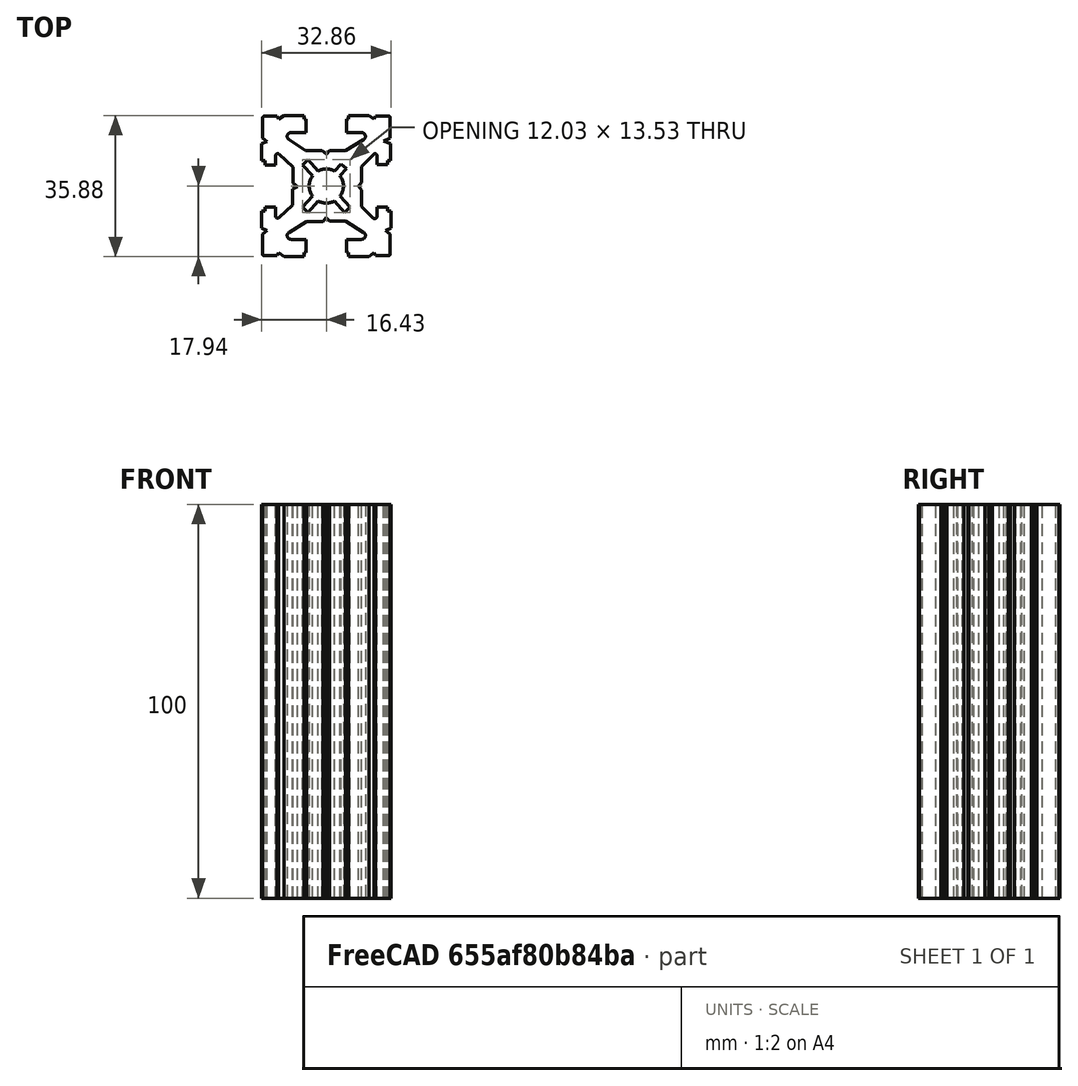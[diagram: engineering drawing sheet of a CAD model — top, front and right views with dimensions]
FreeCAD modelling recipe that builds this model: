
FCSTD DOCUMENT  (FreeCAD 0.17R13509 (Git))
Label: Profile Bosh 30x30mm
License: All rights reserved
LicenseURL: http://en.wikipedia.org/wiki/All_rights_reserved
objects: Sketcher::SketchObject×2, PartDesign::Pad×1, PartDesign::Body×1, App::Part×1
note: 5 computed .brp shape members not serialized (recipe doc carries the construction recipe); baked Part::Feature solids carry a one-line shape summary decoded from their .brp

FEATURE [Sketcher::SketchObject] Sketch
  sketch-geometry (116):
    g0: BSplineCurve PolesCount=2 KnotsCount=2 Degree=1 IsPeriodic=0
    g1: BSplineCurve PolesCount=2 KnotsCount=2 Degree=1 IsPeriodic=0
    g2: BSplineCurve PolesCount=2 KnotsCount=2 Degree=1 IsPeriodic=0
    g3: BSplineCurve PolesCount=3 KnotsCount=2 Degree=2 IsPeriodic=0
    g4: BSplineCurve PolesCount=3 KnotsCount=2 Degree=2 IsPeriodic=0
    g5: BSplineCurve PolesCount=3 KnotsCount=2 Degree=2 IsPeriodic=0
    g6: BSplineCurve PolesCount=3 KnotsCount=2 Degree=2 IsPeriodic=0
    g7: BSplineCurve PolesCount=3 KnotsCount=2 Degree=2 IsPeriodic=0
    g8: BSplineCurve PolesCount=3 KnotsCount=2 Degree=2 IsPeriodic=0
    g9: BSplineCurve PolesCount=3 KnotsCount=2 Degree=2 IsPeriodic=0
    g10: BSplineCurve PolesCount=3 KnotsCount=2 Degree=2 IsPeriodic=0
    g11: BSplineCurve PolesCount=2 KnotsCount=2 Degree=1 IsPeriodic=0
    g12: BSplineCurve PolesCount=2 KnotsCount=2 Degree=1 IsPeriodic=0
    g13: BSplineCurve PolesCount=2 KnotsCount=2 Degree=1 IsPeriodic=0
    g14: BSplineCurve PolesCount=2 KnotsCount=2 Degree=1 IsPeriodic=0
    g15: BSplineCurve PolesCount=2 KnotsCount=2 Degree=1 IsPeriodic=0
    g16: BSplineCurve PolesCount=2 KnotsCount=2 Degree=1 IsPeriodic=0
    g17: BSplineCurve PolesCount=2 KnotsCount=2 Degree=1 IsPeriodic=0
    g18: BSplineCurve PolesCount=2 KnotsCount=2 Degree=1 IsPeriodic=0
    g19: BSplineCurve PolesCount=2 KnotsCount=2 Degree=1 IsPeriodic=0
    g20: BSplineCurve PolesCount=2 KnotsCount=2 Degree=1 IsPeriodic=0
    g21: BSplineCurve PolesCount=2 KnotsCount=2 Degree=1 IsPeriodic=0
    g22: BSplineCurve PolesCount=2 KnotsCount=2 Degree=1 IsPeriodic=0
    g23: BSplineCurve PolesCount=2 KnotsCount=2 Degree=1 IsPeriodic=0
    g24: BSplineCurve PolesCount=2 KnotsCount=2 Degree=1 IsPeriodic=0
    g25: BSplineCurve PolesCount=2 KnotsCount=2 Degree=1 IsPeriodic=0
    g26: BSplineCurve PolesCount=2 KnotsCount=2 Degree=1 IsPeriodic=0
    g27: BSplineCurve PolesCount=2 KnotsCount=2 Degree=1 IsPeriodic=0
    g28: BSplineCurve PolesCount=2 KnotsCount=2 Degree=1 IsPeriodic=0
    g29: BSplineCurve PolesCount=2 KnotsCount=2 Degree=1 IsPeriodic=0
    g30: BSplineCurve PolesCount=2 KnotsCount=2 Degree=1 IsPeriodic=0
    g31: BSplineCurve PolesCount=2 KnotsCount=2 Degree=1 IsPeriodic=0
    g32: BSplineCurve PolesCount=2 KnotsCount=2 Degree=1 IsPeriodic=0
    g33: BSplineCurve PolesCount=2 KnotsCount=2 Degree=1 IsPeriodic=0
    g34: BSplineCurve PolesCount=2 KnotsCount=2 Degree=1 IsPeriodic=0
    g35: BSplineCurve PolesCount=2 KnotsCount=2 Degree=1 IsPeriodic=0
    g36: BSplineCurve PolesCount=2 KnotsCount=2 Degree=1 IsPeriodic=0
    g37: BSplineCurve PolesCount=2 KnotsCount=2 Degree=1 IsPeriodic=0
    g38: BSplineCurve PolesCount=2 KnotsCount=2 Degree=1 IsPeriodic=0
    g39: BSplineCurve PolesCount=2 KnotsCount=2 Degree=1 IsPeriodic=0
    g40: BSplineCurve PolesCount=2 KnotsCount=2 Degree=1 IsPeriodic=0
    g41: BSplineCurve PolesCount=2 KnotsCount=2 Degree=1 IsPeriodic=0
    g42: BSplineCurve PolesCount=2 KnotsCount=2 Degree=1 IsPeriodic=0
    g43: BSplineCurve PolesCount=2 KnotsCount=2 Degree=1 IsPeriodic=0
    g44: BSplineCurve PolesCount=3 KnotsCount=2 Degree=2 IsPeriodic=0
    g45: BSplineCurve PolesCount=2 KnotsCount=2 Degree=1 IsPeriodic=0
    g46: BSplineCurve PolesCount=2 KnotsCount=2 Degree=1 IsPeriodic=0
    g47: BSplineCurve PolesCount=2 KnotsCount=2 Degree=1 IsPeriodic=0
    g48: BSplineCurve PolesCount=2 KnotsCount=2 Degree=1 IsPeriodic=0
    g49: BSplineCurve PolesCount=3 KnotsCount=2 Degree=2 IsPeriodic=0
    g50: BSplineCurve PolesCount=2 KnotsCount=2 Degree=1 IsPeriodic=0
    g51: BSplineCurve PolesCount=3 KnotsCount=2 Degree=2 IsPeriodic=0
    g52: BSplineCurve PolesCount=3 KnotsCount=2 Degree=2 IsPeriodic=0
    g53: BSplineCurve PolesCount=3 KnotsCount=2 Degree=2 IsPeriodic=0
    g54: BSplineCurve PolesCount=2 KnotsCount=2 Degree=1 IsPeriodic=0
    g55: BSplineCurve PolesCount=2 KnotsCount=2 Degree=1 IsPeriodic=0
    g56: BSplineCurve PolesCount=2 KnotsCount=2 Degree=1 IsPeriodic=0
    g57: BSplineCurve PolesCount=2 KnotsCount=2 Degree=1 IsPeriodic=0
    g58: BSplineCurve PolesCount=3 KnotsCount=2 Degree=2 IsPeriodic=0
    g59: BSplineCurve PolesCount=3 KnotsCount=2 Degree=2 IsPeriodic=0
    g60: BSplineCurve PolesCount=3 KnotsCount=2 Degree=2 IsPeriodic=0
    g61: BSplineCurve PolesCount=2 KnotsCount=2 Degree=1 IsPeriodic=0
    g62: BSplineCurve PolesCount=2 KnotsCount=2 Degree=1 IsPeriodic=0
    g63: BSplineCurve PolesCount=2 KnotsCount=2 Degree=1 IsPeriodic=0
    g64: BSplineCurve PolesCount=2 KnotsCount=2 Degree=1 IsPeriodic=0
    g65: BSplineCurve PolesCount=2 KnotsCount=2 Degree=1 IsPeriodic=0
    g66: BSplineCurve PolesCount=2 KnotsCount=2 Degree=1 IsPeriodic=0
    g67: BSplineCurve PolesCount=2 KnotsCount=2 Degree=1 IsPeriodic=0
    g68: BSplineCurve PolesCount=2 KnotsCount=2 Degree=1 IsPeriodic=0
    g69: BSplineCurve PolesCount=2 KnotsCount=2 Degree=1 IsPeriodic=0
    g70: BSplineCurve PolesCount=2 KnotsCount=2 Degree=1 IsPeriodic=0
    g71: BSplineCurve PolesCount=2 KnotsCount=2 Degree=1 IsPeriodic=0
    g72: BSplineCurve PolesCount=2 KnotsCount=2 Degree=1 IsPeriodic=0
    g73: BSplineCurve PolesCount=2 KnotsCount=2 Degree=1 IsPeriodic=0
    g74: BSplineCurve PolesCount=2 KnotsCount=2 Degree=1 IsPeriodic=0
    g75: BSplineCurve PolesCount=2 KnotsCount=2 Degree=1 IsPeriodic=0
    g76: BSplineCurve PolesCount=2 KnotsCount=2 Degree=1 IsPeriodic=0
    g77: BSplineCurve PolesCount=2 KnotsCount=2 Degree=1 IsPeriodic=0
    g78: BSplineCurve PolesCount=2 KnotsCount=2 Degree=1 IsPeriodic=0
    g79: BSplineCurve PolesCount=2 KnotsCount=2 Degree=1 IsPeriodic=0
    g80: BSplineCurve PolesCount=2 KnotsCount=2 Degree=1 IsPeriodic=0
    g81: BSplineCurve PolesCount=2 KnotsCount=2 Degree=1 IsPeriodic=0
    g82: BSplineCurve PolesCount=2 KnotsCount=2 Degree=1 IsPeriodic=0
    g83: BSplineCurve PolesCount=2 KnotsCount=2 Degree=1 IsPeriodic=0
    g84: BSplineCurve PolesCount=2 KnotsCount=2 Degree=1 IsPeriodic=0
    g85: BSplineCurve PolesCount=2 KnotsCount=2 Degree=1 IsPeriodic=0
    g86: BSplineCurve PolesCount=2 KnotsCount=2 Degree=1 IsPeriodic=0
    g87: BSplineCurve PolesCount=2 KnotsCount=2 Degree=1 IsPeriodic=0
    g88: BSplineCurve PolesCount=2 KnotsCount=2 Degree=1 IsPeriodic=0
    g89: BSplineCurve PolesCount=2 KnotsCount=2 Degree=1 IsPeriodic=0
    g90: BSplineCurve PolesCount=2 KnotsCount=2 Degree=1 IsPeriodic=0
    g91: BSplineCurve PolesCount=2 KnotsCount=2 Degree=1 IsPeriodic=0
    g92: BSplineCurve PolesCount=2 KnotsCount=2 Degree=1 IsPeriodic=0
    g93: BSplineCurve PolesCount=2 KnotsCount=2 Degree=1 IsPeriodic=0
    g94: BSplineCurve PolesCount=2 KnotsCount=2 Degree=1 IsPeriodic=0
    g95: BSplineCurve PolesCount=2 KnotsCount=2 Degree=1 IsPeriodic=0
    g96: BSplineCurve PolesCount=2 KnotsCount=2 Degree=1 IsPeriodic=0
    g97: BSplineCurve PolesCount=2 KnotsCount=2 Degree=1 IsPeriodic=0
    g98: BSplineCurve PolesCount=2 KnotsCount=2 Degree=1 IsPeriodic=0
    g99: BSplineCurve PolesCount=2 KnotsCount=2 Degree=1 IsPeriodic=0
    g100: BSplineCurve PolesCount=2 KnotsCount=2 Degree=1 IsPeriodic=0
    g101: BSplineCurve PolesCount=2 KnotsCount=2 Degree=1 IsPeriodic=0
    g102: BSplineCurve PolesCount=2 KnotsCount=2 Degree=1 IsPeriodic=0
    g103: BSplineCurve PolesCount=2 KnotsCount=2 Degree=1 IsPeriodic=0
    g104: BSplineCurve PolesCount=2 KnotsCount=2 Degree=1 IsPeriodic=0
    g105: BSplineCurve PolesCount=2 KnotsCount=2 Degree=1 IsPeriodic=0
    g106: BSplineCurve PolesCount=2 KnotsCount=2 Degree=1 IsPeriodic=0
    g107: BSplineCurve PolesCount=2 KnotsCount=2 Degree=1 IsPeriodic=0
    g108: BSplineCurve PolesCount=2 KnotsCount=2 Degree=1 IsPeriodic=0
    g109: BSplineCurve PolesCount=2 KnotsCount=2 Degree=1 IsPeriodic=0
    g110: BSplineCurve PolesCount=2 KnotsCount=2 Degree=1 IsPeriodic=0
    g111: BSplineCurve PolesCount=2 KnotsCount=2 Degree=1 IsPeriodic=0
    g112: BSplineCurve PolesCount=2 KnotsCount=2 Degree=1 IsPeriodic=0
    g113: BSplineCurve PolesCount=2 KnotsCount=2 Degree=1 IsPeriodic=0
    g114: BSplineCurve PolesCount=2 KnotsCount=2 Degree=1 IsPeriodic=0
    g115: BSplineCurve PolesCount=2 KnotsCount=2 Degree=1 IsPeriodic=0
FEATURE [Sketcher::SketchObject] Sketch001
  MapMode = 5
  Support = -> [XY_Plane001]
  sketch-geometry (121):
    g0: LineSegment [constr] StartX=0 StartY=0 StartZ=0 EndX=0 EndY=8.13256 EndZ=0
    g1: LineSegment [constr] StartX=8.13256 StartY=0 StartZ=0 EndX=0 EndY=0 EndZ=0
    g2: LineSegment StartX=0 StartY=8.13256 StartZ=0 EndX=0.863984 EndY=8.96505 EndZ=0
    g3: LineSegment StartX=0.863984 StartY=8.96505 StartZ=0 EndX=4.93425 EndY=8.96505 EndZ=0
    g4: LineSegment StartX=4.93425 StartY=8.96505 StartZ=0 EndX=9.48637 EndY=11.797 EndZ=0
    g5: LineSegment StartX=8.98459 StartY=13.5535 StartZ=0 EndX=5.15812 EndY=13.5535 EndZ=0
    g6: LineSegment StartX=5.15812 StartY=13.5535 StartZ=0 EndX=5.15812 EndY=16.9407 EndZ=0
    g7: LineSegment StartX=5.15812 StartY=16.9407 StartZ=0 EndX=5.6531 EndY=16.9407 EndZ=0
    g8: LineSegment StartX=5.6531 StartY=16.9407 StartZ=0 EndX=5.6531 EndY=17.9363 EndZ=0
    g9: LineSegment StartX=5.6531 StartY=17.9363 StartZ=0 EndX=10.7923 EndY=17.9363 EndZ=0
    g10: LineSegment StartX=10.7923 StartY=17.9363 StartZ=0 EndX=12.0719 EndY=16.9647 EndZ=0
    g11: LineSegment StartX=12.0719 StartY=16.9647 StartZ=0 EndX=12.5221 EndY=17.7592 EndZ=0
    g12: LineSegment StartX=12.5221 StartY=17.7592 StartZ=0 EndX=15.8708 EndY=17.7592 EndZ=0
    g13: LineSegment StartX=16.246 StartY=17.384 StartZ=0 EndX=16.246 EndY=12.1724 EndZ=0
    g14: LineSegment StartX=16.246 StartY=12.1724 StartZ=0 EndX=14.4892 EndY=11.3845 EndZ=0
    g15: LineSegment StartX=14.4892 StartY=11.3845 StartZ=0 EndX=16.2567 EndY=10.735 EndZ=0
    g16: LineSegment StartX=16.2567 StartY=10.735 StartZ=0 EndX=16.2567 EndY=6.42108 EndZ=0
    g17: LineSegment StartX=16.2567 StartY=6.42108 StartZ=0 EndX=15.6194 EndY=6.42108 EndZ=0
    g18: ArcOfCircle CenterX=15.8708 CenterY=17.384 CenterZ=0 NormalX=0 NormalY=0 NormalZ=1 AngleXU=0 Radius=0.375206 StartAngle=0 EndAngle=1.5708
    g19: ArcOfCircle CenterX=12.38 CenterY=7.66792 CenterZ=0 NormalX=0 NormalY=0 NormalZ=1 AngleXU=0 Radius=0.511001 StartAngle=0 EndAngle=2.35619
    g20: ArcOfCircle CenterX=8.98459 CenterY=12.6036 CenterZ=0 NormalX=0 NormalY=0 NormalZ=1 AngleXU=0 Radius=0.949916 StartAngle=5.26891 EndAngle=7.85398
    g21: LineSegment StartX=15.6194 StartY=6.42108 StartZ=0 EndX=15.6194 EndY=5.37886 EndZ=0
    g22: LineSegment StartX=15.6194 StartY=5.37886 StartZ=0 EndX=12.891 EndY=5.37886 EndZ=0
    g23: LineSegment StartX=12.891 StartY=5.37886 StartZ=0 EndX=12.891 EndY=7.66792 EndZ=0
    g24: LineSegment StartX=12.0187 StartY=8.02925 StartZ=0 EndX=8.94375 EndY=4.95429 EndZ=0
    g25: LineSegment StartX=8.94375 StartY=4.95429 StartZ=0 EndX=8.94375 EndY=0.884017 EndZ=0
    g26: LineSegment StartX=8.94375 StartY=0.884017 StartZ=0 EndX=8.13256 EndY=0 EndZ=0
    g27: ArcOfCircle CenterX=0 CenterY=0 CenterZ=0 NormalX=0 NormalY=0 NormalZ=1 AngleXU=0 Radius=4.34461 StartAngle=1.06729 EndAngle=2.0743
    g28: LineSegment StartX=-2.09626 StartY=3.80544 StartZ=0 EndX=-4.58638 EndY=6.76319 EndZ=0
    g29: LineSegment StartX=-4.58638 StartY=6.76319 StartZ=0 EndX=-6.01301 EndY=5.3625 EndZ=0
    g30: LineSegment StartX=-6.01301 StartY=5.3625 StartZ=0 EndX=-3.47101 EndY=2.61299 EndZ=0
    g31: LineSegment StartX=2.09626 StartY=3.80544 StartZ=0 EndX=3.70713 EndY=5.62355 EndZ=0
    g32: LineSegment StartX=3.70713 StartY=5.62355 StartZ=0 EndX=5.08583 EndY=4.45696 EndZ=0
    g33: LineSegment StartX=5.08583 StartY=4.45696 StartZ=0 EndX=3.47101 EndY=2.61299 EndZ=0
    g34: LineSegment StartX=2.09626 StartY=-3.80544 StartZ=0 EndX=4.58638 EndY=-6.76319 EndZ=0
    g35: LineSegment StartX=4.58638 StartY=-6.76319 StartZ=0 EndX=6.01301 EndY=-5.3625 EndZ=0
    g36: LineSegment StartX=6.01301 StartY=-5.3625 StartZ=0 EndX=3.47101 EndY=-2.61299 EndZ=0
    g37: LineSegment StartX=-2.09626 StartY=-3.80544 StartZ=0 EndX=-4.58638 EndY=-6.76319 EndZ=0
    g38: LineSegment StartX=-6.01301 StartY=-5.3625 StartZ=0 EndX=-3.47101 EndY=-2.61299 EndZ=0
    g39: LineSegment StartX=-4.58638 StartY=-6.76319 StartZ=0 EndX=-6.01301 EndY=-5.3625 EndZ=0
    g40: ArcOfCircle CenterX=0 CenterY=0 CenterZ=0 NormalX=0 NormalY=0 NormalZ=1 AngleXU=0 Radius=4.34461 StartAngle=2.4963 EndAngle=3.78689
    g41: ArcOfCircle CenterX=0 CenterY=0 CenterZ=0 NormalX=0 NormalY=0 NormalZ=1 AngleXU=0 Radius=4.34461 StartAngle=4.20889 EndAngle=5.21589
    g42: ArcOfCircle CenterX=0 CenterY=0 CenterZ=0 NormalX=0 NormalY=0 NormalZ=1 AngleXU=0 Radius=4.34461 StartAngle=5.63789 EndAngle=6.92848
    g43: LineSegment [constr] StartX=8.94375 StartY=4.95429 StartZ=0 EndX=10.2141 EndY=4.95429 EndZ=0
    g44: LineSegment StartX=0 StartY=8.13256 StartZ=0 EndX=-1.12485 EndY=9.01316 EndZ=0
    g45: LineSegment StartX=-1.12485 StartY=9.01316 StartZ=0 EndX=-5.23766 EndY=9.01316 EndZ=0
    g46: LineSegment StartX=-5.23766 StartY=9.01316 StartZ=0 EndX=-9.50558 EndY=11.8091 EndZ=0
    g47: LineSegment StartX=-8.98499 StartY=13.5537 StartZ=0 EndX=-5.15812 EndY=13.5537 EndZ=0
    g48: LineSegment StartX=-5.15812 StartY=13.5537 StartZ=0 EndX=-5.15812 EndY=16.9407 EndZ=0
    g49: LineSegment StartX=-5.15812 StartY=16.9407 StartZ=0 EndX=-5.6531 EndY=16.9407 EndZ=0
    g50: LineSegment StartX=-5.6531 StartY=16.9407 StartZ=0 EndX=-5.6531 EndY=17.9363 EndZ=0
    g51: LineSegment StartX=-5.6531 StartY=17.9363 StartZ=0 EndX=-10.7923 EndY=17.9363 EndZ=0
    g52: LineSegment StartX=-10.7923 StartY=17.9363 StartZ=0 EndX=-12.0719 EndY=16.9647 EndZ=0
    g53: LineSegment StartX=-12.0719 StartY=16.9647 StartZ=0 EndX=-12.5221 EndY=17.7251 EndZ=0
    g54: LineSegment StartX=-12.5221 StartY=17.7251 StartZ=0 EndX=-15.8282 EndY=17.7251 EndZ=0
    g55: LineSegment StartX=-16.1524 StartY=17.401 StartZ=0 EndX=-16.1524 EndY=12.1805 EndZ=0
    g56: LineSegment StartX=-16.1524 StartY=12.1805 StartZ=0 EndX=-14.9921 EndY=11.3367 EndZ=0
    g57: LineSegment StartX=-14.9921 StartY=11.3367 StartZ=0 EndX=-16.4328 EndY=10.7136 EndZ=0
    g58: LineSegment StartX=-16.4328 StartY=10.7136 StartZ=0 EndX=-16.4328 EndY=6.42108 EndZ=0
    g59: LineSegment StartX=-16.4328 StartY=6.42108 StartZ=0 EndX=-15.6194 EndY=6.42108 EndZ=0
    g60: ArcOfCircle CenterX=-15.8282 CenterY=17.401 CenterZ=0 NormalX=0 NormalY=0 NormalZ=1 AngleXU=0 Radius=0.324122 StartAngle=1.5708 EndAngle=3.14159
    g61: ArcOfCircle CenterX=-8.98499 CenterY=12.6037 CenterZ=0 NormalX=0 NormalY=0 NormalZ=1 AngleXU=0 Radius=0.949992 StartAngle=1.5708 EndAngle=4.13243
    g62: LineSegment StartX=-15.6194 StartY=6.42108 StartZ=0 EndX=-15.6194 EndY=5.3545 EndZ=0
    g63: LineSegment StartX=-15.6194 StartY=5.3545 StartZ=0 EndX=-12.8911 EndY=5.3545 EndZ=0
    g64: ArcOfCircle CenterX=-12.3588 CenterY=7.67266 CenterZ=0 NormalX=0 NormalY=0 NormalZ=1 AngleXU=0 Radius=0.532302 StartAngle=0.822691 EndAngle=3.14117
    g65: LineSegment StartX=-11.9967 StartY=8.06282 StartZ=0 EndX=-8.50501 EndY=4.82235 EndZ=0
    g66: LineSegment StartX=-8.50501 StartY=4.82235 StartZ=0 EndX=-8.50501 EndY=0.709539 EndZ=0
    g67: LineSegment StartX=-8.50501 StartY=0.709539 StartZ=0 EndX=-7.362 EndY=-0.147361 EndZ=0
    g68: LineSegment [constr] StartX=-0.0366578 StartY=0 StartZ=0 EndX=-0.0366578 EndY=-7.97192 EndZ=0
    g69: LineSegment StartX=-0.0366578 StartY=-7.97192 StartZ=0 EndX=0.851967 EndY=-8.95417 EndZ=0
    g70: LineSegment StartX=0.851967 StartY=-8.95417 StartZ=0 EndX=4.95077 EndY=-8.95417 EndZ=0
    g71: LineSegment StartX=4.95077 StartY=-8.95417 StartZ=0 EndX=9.48868 EndY=-11.7973 EndZ=0
    g72: LineSegment StartX=8.98403 StartY=-13.5532 StartZ=0 EndX=5.15812 EndY=-13.5532 EndZ=0
    g73: LineSegment StartX=5.15812 StartY=-13.5532 StartZ=0 EndX=5.15812 EndY=-16.9407 EndZ=0
    g74: LineSegment StartX=5.15812 StartY=-16.9407 StartZ=0 EndX=5.6531 EndY=-16.9407 EndZ=0
    g75: LineSegment StartX=5.6531 StartY=-16.9407 StartZ=0 EndX=5.6531 EndY=-17.9363 EndZ=0
    g76: LineSegment StartX=5.6531 StartY=-17.9363 StartZ=0 EndX=10.7923 EndY=-17.9363 EndZ=0
    g77: LineSegment StartX=10.7923 StartY=-17.9363 StartZ=0 EndX=12.0719 EndY=-16.9647 EndZ=0
    g78: LineSegment StartX=12.0719 StartY=-16.9647 StartZ=0 EndX=12.5221 EndY=-17.7251 EndZ=0
    g79: LineSegment StartX=12.5221 StartY=-17.7251 StartZ=0 EndX=15.8282 EndY=-17.7251 EndZ=0
    g80: LineSegment StartX=16.1524 StartY=-17.401 StartZ=0 EndX=16.1524 EndY=-12.1805 EndZ=0
    g81: LineSegment StartX=16.1524 StartY=-12.1805 StartZ=0 EndX=14.9921 EndY=-11.3367 EndZ=0
    g82: LineSegment StartX=14.9921 StartY=-11.3367 StartZ=0 EndX=16.4328 EndY=-10.7136 EndZ=0
    g83: LineSegment StartX=16.4328 StartY=-10.7136 StartZ=0 EndX=16.4328 EndY=-6.42108 EndZ=0
    g84: ArcOfCircle CenterX=15.8282 CenterY=-17.401 CenterZ=0 NormalX=0 NormalY=0 NormalZ=1 AngleXU=0 Radius=0.324122 StartAngle=4.71239 EndAngle=6.28319
    g85: ArcOfCircle CenterX=12.2781 CenterY=-7.67162 CenterZ=0 NormalX=0 NormalY=0 NormalZ=1 AngleXU=0 Radius=0.613906 StartAngle=3.92699 EndAngle=6.28319
    g86: ArcOfCircle CenterX=8.98403 CenterY=-12.6027 CenterZ=0 NormalX=0 NormalY=0 NormalZ=1 AngleXU=0 Radius=0.950502 StartAngle=4.71239 EndAngle=7.29429
    g87: LineSegment StartX=12.892 StartY=-5.37886 StartZ=0 EndX=12.892 EndY=-7.67162 EndZ=0
    g88: LineSegment StartX=11.844 StartY=-8.10572 StartZ=0 EndX=8.9097 EndY=-5.17142 EndZ=0
    g89: LineSegment StartX=-0.0366578 StartY=-7.97192 StartZ=0 EndX=-0.845387 EndY=-8.98483 EndZ=0
    g90: LineSegment StartX=-0.845387 StartY=-8.98483 StartZ=0 EndX=-4.96492 EndY=-8.98483 EndZ=0
    g91: LineSegment StartX=-4.96492 StartY=-8.98483 StartZ=0 EndX=-9.48593 EndY=-11.7955 EndZ=0
    g92: LineSegment StartX=-8.98406 StartY=-13.5533 StartZ=0 EndX=-5.15812 EndY=-13.5533 EndZ=0
    g93: LineSegment StartX=-5.15812 StartY=-13.5533 StartZ=0 EndX=-5.15812 EndY=-16.9407 EndZ=0
    g94: LineSegment StartX=-5.15812 StartY=-16.9407 StartZ=0 EndX=-5.6531 EndY=-16.9407 EndZ=0
    g95: LineSegment StartX=-5.6531 StartY=-16.9407 StartZ=0 EndX=-5.6531 EndY=-17.9363 EndZ=0
    g96: LineSegment StartX=-5.6531 StartY=-17.9363 StartZ=0 EndX=-10.7923 EndY=-17.9363 EndZ=0
    g97: LineSegment StartX=-10.7923 StartY=-17.9363 StartZ=0 EndX=-12.0719 EndY=-16.9647 EndZ=0
    g98: LineSegment StartX=-12.0719 StartY=-16.9647 StartZ=0 EndX=-12.5221 EndY=-17.7251 EndZ=0
    g99: LineSegment StartX=-12.5221 StartY=-17.7251 StartZ=0 EndX=-15.8282 EndY=-17.7251 EndZ=0
    g100: LineSegment StartX=-16.1524 StartY=-17.401 StartZ=0 EndX=-16.1524 EndY=-12.1805 EndZ=0
    g101: LineSegment StartX=-16.1524 StartY=-12.1805 StartZ=0 EndX=-14.9921 EndY=-11.3367 EndZ=0
    g102: LineSegment StartX=-14.9921 StartY=-11.3367 StartZ=0 EndX=-16.4328 EndY=-10.7136 EndZ=0
    g103: LineSegment StartX=-16.4328 StartY=-10.7136 StartZ=0 EndX=-16.4328 EndY=-6.42108 EndZ=0
    g104: ArcOfCircle CenterX=-15.8282 CenterY=-17.401 CenterZ=0 NormalX=0 NormalY=0 NormalZ=1 AngleXU=0 Radius=0.324122 StartAngle=3.14159 EndAngle=4.71239
    g105: ArcOfCircle CenterX=-8.98406 CenterY=-12.6028 CenterZ=0 NormalX=0 NormalY=0 NormalZ=1 AngleXU=0 Radius=0.950558 StartAngle=2.12701 EndAngle=4.71239
    g106: ArcOfCircle CenterX=-12.3712 CenterY=-7.67362 CenterZ=0 NormalX=0 NormalY=0 NormalZ=1 AngleXU=0 Radius=0.522418 StartAngle=3.14233 EndAngle=5.45425
    g107: LineSegment StartX=-12.0182 StartY=-8.05875 StartZ=0 EndX=-8.51881 EndY=-4.85154 EndZ=0
    g108: LineSegment StartX=16.4328 StartY=-6.42108 StartZ=0 EndX=15.6194 EndY=-6.42108 EndZ=0
    g109: LineSegment StartX=15.6194 StartY=-6.42108 StartZ=0 EndX=15.6194 EndY=-5.37886 EndZ=0
    g110: LineSegment StartX=15.6194 StartY=-5.37886 StartZ=0 EndX=12.892 EndY=-5.37886 EndZ=0
    g111: LineSegment StartX=8.9097 StartY=-5.17142 StartZ=0 EndX=8.9097 EndY=-1.07262 EndZ=0
    g112: LineSegment StartX=8.9097 StartY=-1.07262 StartZ=0 EndX=8.13256 EndY=0 EndZ=0
    g113: LineSegment [constr] StartX=8.9097 StartY=-5.17142 StartZ=0 EndX=10.2141 EndY=-5.17142 EndZ=0
    g114: LineSegment StartX=-16.4328 StartY=-6.42108 StartZ=0 EndX=-15.6194 EndY=-6.42108 EndZ=0
    g115: LineSegment StartX=-15.6194 StartY=-6.42108 StartZ=0 EndX=-15.6194 EndY=-5.37886 EndZ=0
    g116: LineSegment StartX=-15.6194 StartY=-5.37886 StartZ=0 EndX=-12.8936 EndY=-5.37886 EndZ=0
    g117: LineSegment StartX=-8.51881 StartY=-4.85154 StartZ=0 EndX=-8.51881 EndY=-0.732016 EndZ=0
    g118: LineSegment StartX=-8.51881 StartY=-0.732016 StartZ=0 EndX=-7.362 EndY=-0.147361 EndZ=0
    g119: LineSegment StartX=-12.8911 StartY=7.67288 StartZ=0 EndX=-12.8911 EndY=5.3545 EndZ=0
    g120: LineSegment StartX=-12.8936 StartY=-5.37886 StartZ=0 EndX=-12.8936 EndY=-7.674 EndZ=0
  constraints (200):
    c: PointOnObject(g0,g-2)
    c: Coincident(g-1,g0)
    c: Coincident(g1,g0)
    c: Horizontal(g1)
    c: Equal(g1,g0)
    c: Coincident(g2,g3)
    c: Horizontal(g3)
    c: Coincident(g3,g4)
    c: Horizontal(g5)
    c: Coincident(g5,g6)
    c: Vertical(g6)
    c: Coincident(g6,g7)
    c: Horizontal(g7)
    c: Coincident(g7,g8)
    c: Coincident(g8,g9)
    c: Horizontal(g9)
    c: Coincident(g9,g10)
    c: Coincident(g10,g11)
    c: Coincident(g11,g12)
    c: Horizontal(g12)
    c: Vertical(g13)
    c: Coincident(g13,g14)
    c: Coincident(g14,g15)
    c: Coincident(g15,g16)
    c: Vertical(g16)
    c: Coincident(g16,g17)
    c: Horizontal(g17)
    c: Coincident(g17,g21)
    c: Coincident(g21,g22)
    c: Horizontal(g22)
    c: Coincident(g22,g23)
    c: Vertical(g23)
    c: Coincident(g24,g25)
    c: Vertical(g25)
    c: Coincident(g25,g26)
    c: Tangent(g12,g18) = 1.5708
    c: Tangent(g13,g18) = 1.5708
    c: Tangent(g23,g19) = -1.5708
    c: Tangent(g24,g19) = -1.5708
    c: Tangent(g4,g20) = -1.5708
    c: Tangent(g5,g20) = -1.5708
    c: Coincident(g1,g26)
    c: Vertical(g8)
    c: Coincident(g27,g-1)
    c: Coincident(g31,g32)
    c: Coincident(g32,g33)
    c: Coincident(g34,g35)
    c: Coincident(g35,g36)
    c: PointOnObject(g38,g27)
    c: PointOnObject(g37,g27)
    c: PointOnObject(g34,g27)
    c: PointOnObject(g36,g27)
    c: Coincident(g27,g31)
    c: Coincident(g42,g33)
    c: Equal(g27,g40)
    c: Coincident(g27,g40)
    c: Equal(g40,g41)
    c: PointOnObject(g40,g38)
    c: PointOnObject(g41,g37)
    c: Coincident(g40,g41)
    c: Equal(g41,g42)
    c: PointOnObject(g41,g34)
    c: PointOnObject(g42,g36)
    c: Coincident(g41,g42)
    c: Vertical(g21)
    c: Coincident(g24,g43)
    c: Horizontal(g43)
    c: Angle(g43,g24) = 0.785398
    c: Coincident(g0,g2)
    c: Equal(g25,g3)
    c: Equal(g26,g2)
    c: Coincident(g44,g45)
    c: Horizontal(g45)
    c: Coincident(g45,g46)
    c: Horizontal(g47)
    c: Coincident(g47,g48)
    c: Vertical(g48)
    c: Coincident(g48,g49)
    c: Horizontal(g49)
    c: Coincident(g49,g50)
    c: Coincident(g50,g51)
    c: Horizontal(g51)
    c: Coincident(g51,g52)
    c: Coincident(g52,g53)
    c: Coincident(g53,g54)
    c: Horizontal(g54)
    c: Vertical(g55)
    c: Coincident(g55,g56)
    c: Coincident(g56,g57)
    c: Coincident(g57,g58)
    c: Vertical(g58)
    c: Coincident(g58,g59)
    c: Horizontal(g59)
    c: Coincident(g59,g62)
    c: Coincident(g62,g63)
    c: Horizontal(g63)
    c: Coincident(g65,g66)
    c: Vertical(g66)
    c: Coincident(g66,g67)
    c: Tangent(g54,g60) = -1.5708
    c: Tangent(g55,g60) = -1.5708
    c: Tangent(g65,g64) = 1.5708
    c: Tangent(g46,g61) = 1.5708
    c: Tangent(g47,g61) = 1.5708
    c: Vertical(g50)
    c: Vertical(g62)
    c: Equal(g66,g45)
    c: Equal(g67,g44)
    c: Coincident(g44,g0)
    c: Coincident(g69,g70)
    c: Horizontal(g70)
    c: Coincident(g70,g71)
    c: Horizontal(g72)
    c: Coincident(g72,g73)
    c: Vertical(g73)
    c: Coincident(g73,g74)
    c: Horizontal(g74)
    c: Coincident(g74,g75)
    c: Coincident(g75,g76)
    c: Horizontal(g76)
    c: Coincident(g76,g77)
    c: Coincident(g77,g78)
    c: Coincident(g78,g79)
    c: Horizontal(g79)
    c: Vertical(g80)
    c: Coincident(g80,g81)
    c: Coincident(g81,g82)
    c: Coincident(g82,g83)
    c: Vertical(g83)
    c: Coincident(g83,g108)
    c: Horizontal(g108)
    c: Coincident(g108,g109)
    c: Coincident(g109,g110)
    c: Horizontal(g110)
    c: Coincident(g110,g87)
    c: Vertical(g87)
    c: Coincident(g88,g111)
    c: Vertical(g111)
    c: Coincident(g111,g112)
    c: Tangent(g79,g84) = -1.5708
    c: Tangent(g80,g84) = -1.5708
    c: Tangent(g87,g85) = 1.5708
    c: Tangent(g88,g85) = 1.5708
    c: Tangent(g71,g86) = 1.5708
    c: Tangent(g72,g86) = 1.5708
    c: Vertical(g75)
    c: Vertical(g109)
    c: Coincident(g88,g113)
    c: Horizontal(g113)
    c: Angle(g113,g88) = -0.785398
    c: Coincident(g68,g69)
    c: Equal(g111,g70)
    c: Equal(g112,g69)
    c: Coincident(g89,g90)
    c: Horizontal(g90)
    c: Coincident(g90,g91)
    c: Horizontal(g92)
    c: Coincident(g92,g93)
    c: Vertical(g93)
    c: Coincident(g93,g94)
    c: Horizontal(g94)
    c: Coincident(g94,g95)
    c: Coincident(g95,g96)
    c: Horizontal(g96)
    c: Coincident(g96,g97)
    c: Coincident(g97,g98)
    c: Coincident(g98,g99)
    c: Horizontal(g99)
    c: Vertical(g100)
    c: Coincident(g100,g101)
    c: Coincident(g101,g102)
    c: Coincident(g102,g103)
    c: Vertical(g103)
    c: Coincident(g103,g114)
    c: Horizontal(g114)
    c: Coincident(g114,g115)
    c: Coincident(g115,g116)
    c: Horizontal(g116)
    c: Coincident(g107,g117)
    c: Vertical(g117)
    c: Coincident(g117,g118)
    c: Tangent(g99,g104) = 1.5708
    c: Tangent(g100,g104) = 1.5708
    c: Tangent(g107,g106) = -1.5708
    c: Tangent(g91,g105) = -1.5708
    c: Tangent(g92,g105) = -1.5708
    c: Vertical(g95)
    c: Vertical(g115)
    c: Equal(g117,g90)
    c: Equal(g118,g89)
    c: Coincident(g89,g68)
    c: Coincident(g112,g1)
    c: Coincident(g67,g118)
    c: Vertical(g68)
    c: Coincident(g119,g63)
    c: Vertical(g119)
    c: Coincident(g119,g64)
    c: Coincident(g116,g120)
    c: Coincident(g120,g106)
    c: Vertical(g120)
FEATURE [PartDesign::Pad] Pad
  Length = 100
  Length2 = 100
  Profile = -> Sketch001
  Refine = true
  Type = 0
FEATURE [PartDesign::Body] Body
  Group = -> [Sketch001,Pad]
  Origin = -> Origin001
  Tip = -> Pad
FEATURE [App::Part] Part
  Group = -> [Body]
  License = CC BY 3.0
  LicenseURL = http://creativecommons.org/licenses/by/3.0/
  Origin = -> Origin
